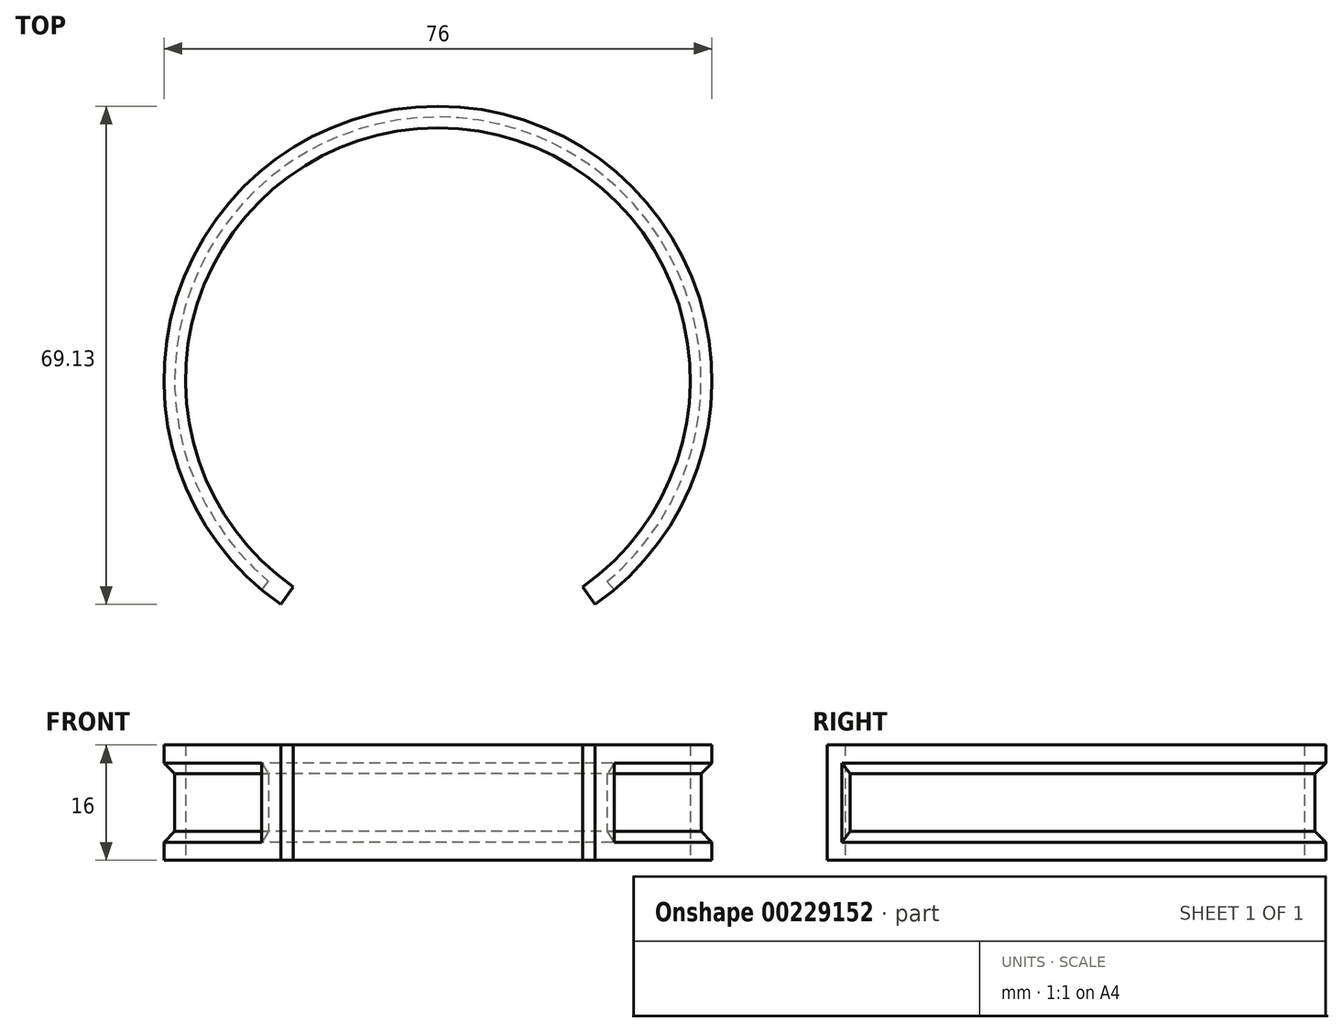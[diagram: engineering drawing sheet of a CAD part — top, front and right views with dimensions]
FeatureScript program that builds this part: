
annotation { "Feature Type Name" : "Feature", "Feature Type Description" : "" }
export const myFeature = defineFeature(function(context is Context, id is Id, definition is map)
    precondition{}
    {
        {
            var Q0;
            Q0=qCreatedBy(makeId("Top.planeOp"),FACE);
            var sketch = newSketch(context, id + "F0", { "sketchPlane" : qUnion([Q0])});
            skArc(sketch, "E0", {"start": v(21.8, -31.13) * mm, "mid": v(37.86, 3.31) * mm, "end": v(16.06, 34.44) * mm});
            skArc(sketch, "E1", {"start": v(20.08, -28.67) * mm, "mid": v(0, 35) * mm, "end": v(-20.08, -28.67) * mm});
            skLineSegment(sketch, "E2", {"start": v(20.08, -28.67) * mm, "end": v(21.8, -31.13) * mm});
            skLineSegment(sketch, "E3", {"start": v(0, -60.58) * mm, "end": v(0, 54.66) * mm, "construction": true});
            skLineSegment(sketch, "E4.MirrorCS", {"start": v(-20.08, -28.67) * mm, "end": v(-21.8, -31.13) * mm});
            skLineSegment(sketch, "E5", {"start": v(-16.06, 34.44) * mm, "end": v(-18.73, 40.16) * mm});
            skLineSegment(sketch, "E6", {"start": v(-37.86, -3.31) * mm, "end": v(-44.14, -3.86) * mm});
            skLineSegment(sketch, "E7", {"start": v(0, 0) * mm, "end": v(-69.84, -40.32) * mm, "construction": true});
            skArc(sketch, "E8.trimOffspring", {"start": v(-16.06, 34.44) * mm, "mid": v(-37.86, 3.31) * mm, "end": v(-21.8, -31.13) * mm});
            skLineSegment(sketch, "E9.MirrorCS", {"start": v(16.06, 34.44) * mm, "end": v(18.73, 40.16) * mm});
            skLineSegment(sketch, "E10.MirrorCS", {"start": v(37.86, -3.31) * mm, "end": v(44.14, -3.86) * mm});
            skArc(sketch, "E11.trimOffspring", {"start": v(16.06, 34.44) * mm, "mid": v(0, 38) * mm, "end": v(-16.06, 34.44) * mm});
            skPoint(sketch, "E12.orphan", {"position": v(-14.8, 31.72) * mm});
            skPoint(sketch, "E13.orphan", {"position": v(14.8, 31.72) * mm});
            skPoint(sketch, "E14.orphan", {"position": v(-34.87, -3.05) * mm});
            skPoint(sketch, "E15.orphan", {"position": v(34.87, -3.05) * mm});
            skPoint(sketch, "E16.visualSharp", {"position": v(-18.73, 40.16) * mm});
            skPoint(sketch, "E17.visualSharp", {"position": v(18.73, 40.16) * mm});
            skPoint(sketch, "E18.visualSharp", {"position": v(44.14, -3.86) * mm});
            skPoint(sketch, "E19.visualSharp", {"position": v(-44.14, -3.86) * mm});
            skSolve(sketch);
        }
        {
            var Q0;
            Q0=qSketchRegion(id+"F0",true);
            extrude(context, id + "F1", {"entities" : qUnion([Q0]), "depth" : 16 * mm, "offsetDistance" : 25 * mm});
        }
        {
            var Q0;
            Q0=qCreatedBy(makeId("Front.planeOp"),FACE);
            var sketch = newSketch(context, id + "F2", { "sketchPlane" : qUnion([Q0])});
            skLineSegment(sketch, "E20", {"start": v(0, -36.51) * mm, "end": v(0, 59.07) * mm, "construction": true});
            skSolve(sketch);
        }
        {
            var Q0;
            Q0=qCreatedBy(makeId("Right.planeOp"),FACE);
            var sketch = newSketch(context, id + "F3", { "sketchPlane" : qUnion([Q0])});
            skLineSegment(sketch, "E21", {"start": v(43.44, 7.71) * mm, "end": v(34.46, 7.71) * mm, "construction": true});
            skLineSegment(sketch, "E22", {"start": v(38, 14.47) * mm, "end": v(38, 13.5) * mm});
            skLineSegment(sketch, "E23", {"start": v(38, 13.5) * mm, "end": v(36.5, 12) * mm});
            skLineSegment(sketch, "E24", {"start": v(36.5, 12) * mm, "end": v(36.5, 4) * mm});
            skLineSegment(sketch, "E25", {"start": v(36.5, 4) * mm, "end": v(38, 2.5) * mm});
            skLineSegment(sketch, "E26", {"start": v(38, 2.5) * mm, "end": v(38, 0) * mm});
            skLineSegment(sketch, "E27", {"start": v(38, 0) * mm, "end": v(42.5, 0) * mm});
            skLineSegment(sketch, "E28", {"start": v(42.5, 0) * mm, "end": v(42.5, 14.64) * mm});
            skLineSegment(sketch, "E29", {"start": v(42.5, 14.64) * mm, "end": v(38, 14.47) * mm});
            skLineSegment(sketch, "E30", {"start": v(38, 22.75) * mm, "end": v(38, -9.84) * mm, "construction": true});
            skSolve(sketch);
        }
        {
            var Q0;
            Q0 = qSketchRegion(id + "F3", true);
            var Q1;
            Q1=sQuery(id+"F2.wireOp",EDGE,"E20");
            revolve(context, id + "F4", {"operationType" : NewBodyOperationType.REMOVE, "surfaceOperationType" : NewSurfaceOperationType.NEW, "entities" : qUnion([Q0]), "axis" : qUnion([Q1]), "revolveType" : RevolveType.SYMMETRIC, "oppositeDirection" : true, "angle" : 280 * degree});
        }
    });
